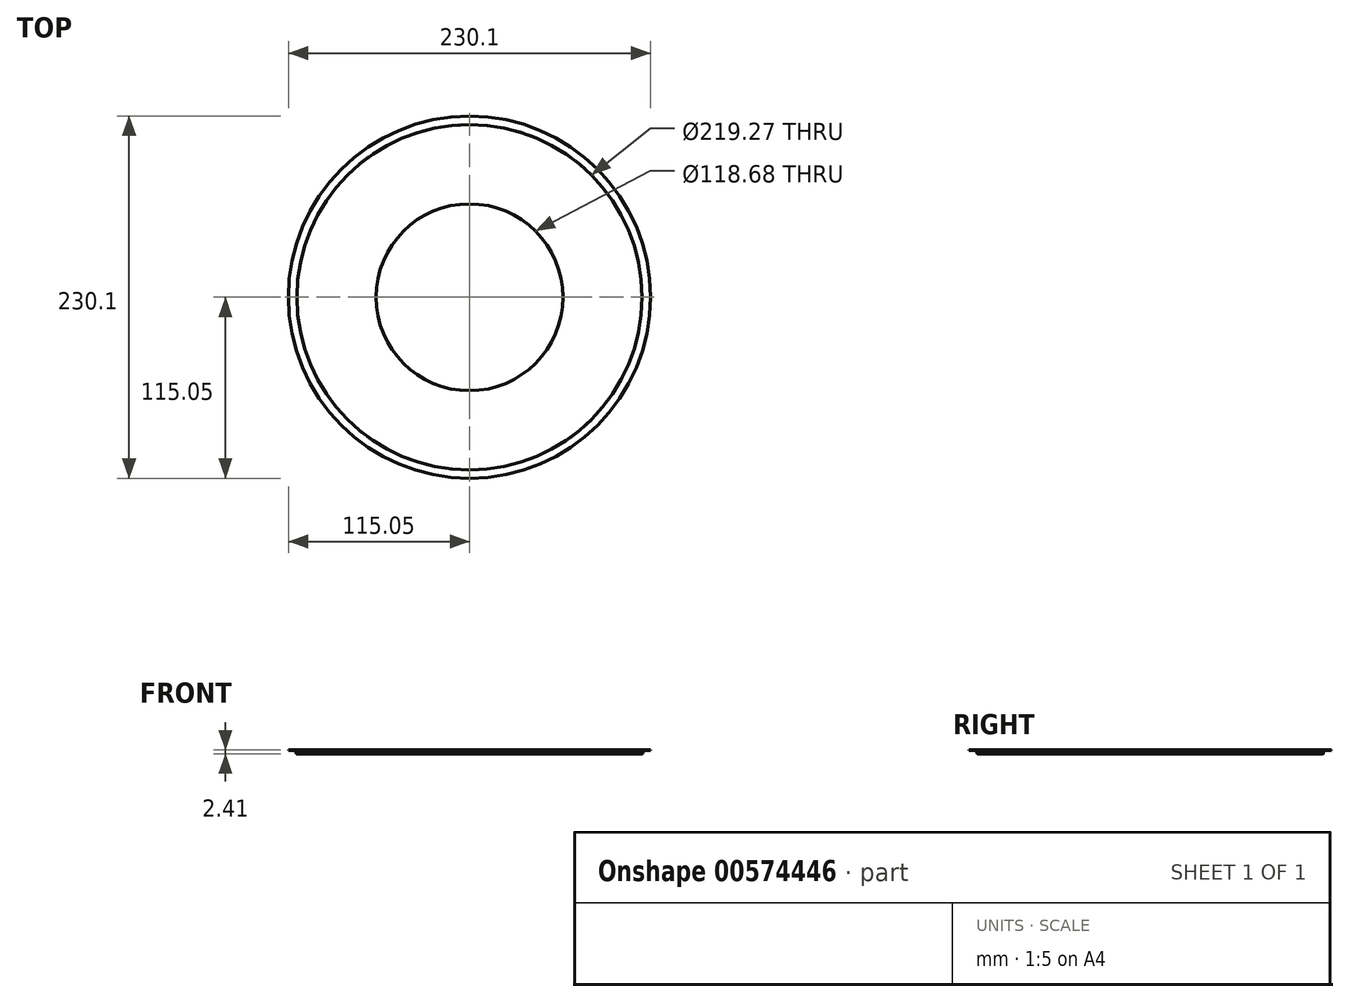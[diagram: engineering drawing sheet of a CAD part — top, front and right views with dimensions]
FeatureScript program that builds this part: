
annotation { "Feature Type Name" : "Feature", "Feature Type Description" : "" }
export const myFeature = defineFeature(function(context is Context, id is Id, definition is map)
    precondition{}
    {
        {
            var Q0;
            Q0=qCreatedBy(makeId("Front.planeOp"),FACE);
            var sketch = newSketch(context, id + "F0", { "sketchPlane" : qUnion([Q0])});
            skLineSegment(sketch, "E0.bottom", {"start": v(0, 0) * mm, "end": v(109.54, 0) * mm});
            skLineSegment(sketch, "E0.top", {"start": v(0, 0.41) * mm, "end": v(109.54, 0.41) * mm});
            skLineSegment(sketch, "E0.left", {"start": v(0, 0) * mm, "end": v(0, 0.41) * mm});
            skLineSegment(sketch, "E1", {"start": v(110.83, 2) * mm, "end": v(115.05, 2) * mm});
            skLineSegment(sketch, "E2", {"start": v(115.05, 2) * mm, "end": v(115.05, 2.41) * mm});
            skLineSegment(sketch, "E3", {"start": v(115.05, 2.41) * mm, "end": v(110.17, 2.41) * mm});
            skLineSegment(sketch, "E4", {"start": v(110.05, 1.88) * mm, "end": v(110.05, 0.5) * mm});
            skLineSegment(sketch, "E5", {"start": v(109.63, 1.88) * mm, "end": v(109.63, 0.5) * mm});
            skLineSegment(sketch, "E6", {"start": v(110.83, 2) * mm, "end": v(110.17, 2) * mm});
            skPoint(sketch, "E7.visualSharp", {"position": v(109.63, 0.41) * mm});
            skArc(sketch, "E7.filletArc", {"start": v(109.54, 0.41) * mm, "mid": v(109.6, 0.44) * mm, "end": v(109.63, 0.5) * mm});
            skArc(sketch, "E8.filletArc", {"start": v(109.54, 0) * mm, "mid": v(109.9, 0.15) * mm, "end": v(110.05, 0.5) * mm});
            skPoint(sketch, "E9.visualSharp", {"position": v(110.05, 2) * mm});
            skArc(sketch, "E9.filletArc", {"start": v(110.17, 2) * mm, "mid": v(110.08, 1.96) * mm, "end": v(110.05, 1.88) * mm});
            skPoint(sketch, "E10.visualSharp", {"position": v(109.63, 2.41) * mm});
            skArc(sketch, "E10.filletArc", {"start": v(110.17, 2.41) * mm, "mid": v(109.8, 2.26) * mm, "end": v(109.63, 1.88) * mm});
            skSolve(sketch);
        }
        {
            var Q0;
            Q0=makeQuery(id+"F0.imprint","IMPRINT",FACE,{"disambiguationData":[TD([[makeQuery(id+"F0.imprint","IMPRINT",EDGE,{"derivedFrom":sQuery(id+"F0.wireOp",EDGE,"E0.bottom")}),1.0]])]});
            var Q1;
            Q1=sQuery(id+"F0.wireOp",EDGE,"E0.left");
            revolve(context, id + "F1", {"entities" : qUnion([Q0]), "axis" : qUnion([Q1]), "revolveType" : RevolveType.FULL});
        }
        {
            var Q0;
            Q0=makeQuery(id+"F1.opRevolve","SWEPT_FACE",FACE,{"disambiguationData":[OSD([sQuery(id+"F0.wireOp",EDGE,"E0.top")])]});
            var sketch = newSketch(context, id + "F2", { "sketchPlane" : qUnion([Q0])});
            skCircle(sketch, "E11", {"center": v(0, 0) * mm, "radius": 59.34 * mm});
            skSolve(sketch);
        }
        {
            var Q0;
            Q0=makeQuery(id+"F2.imprint","IMPRINT",FACE,{"disambiguationData":[TD([[makeQuery(id+"F2.imprint","IMPRINT",EDGE,{"derivedFrom":sQuery(id+"F2.wireOp",EDGE,"E11")}),1.0]])]});
            extrude(context, id + "F3", {"entities" : qUnion([Q0]), "operationType" : NewBodyOperationType.REMOVE, "oppositeDirection" : true, "depth" : 25.4 * mm, "offsetDistance" : 25.4 * mm});
        }
    });
